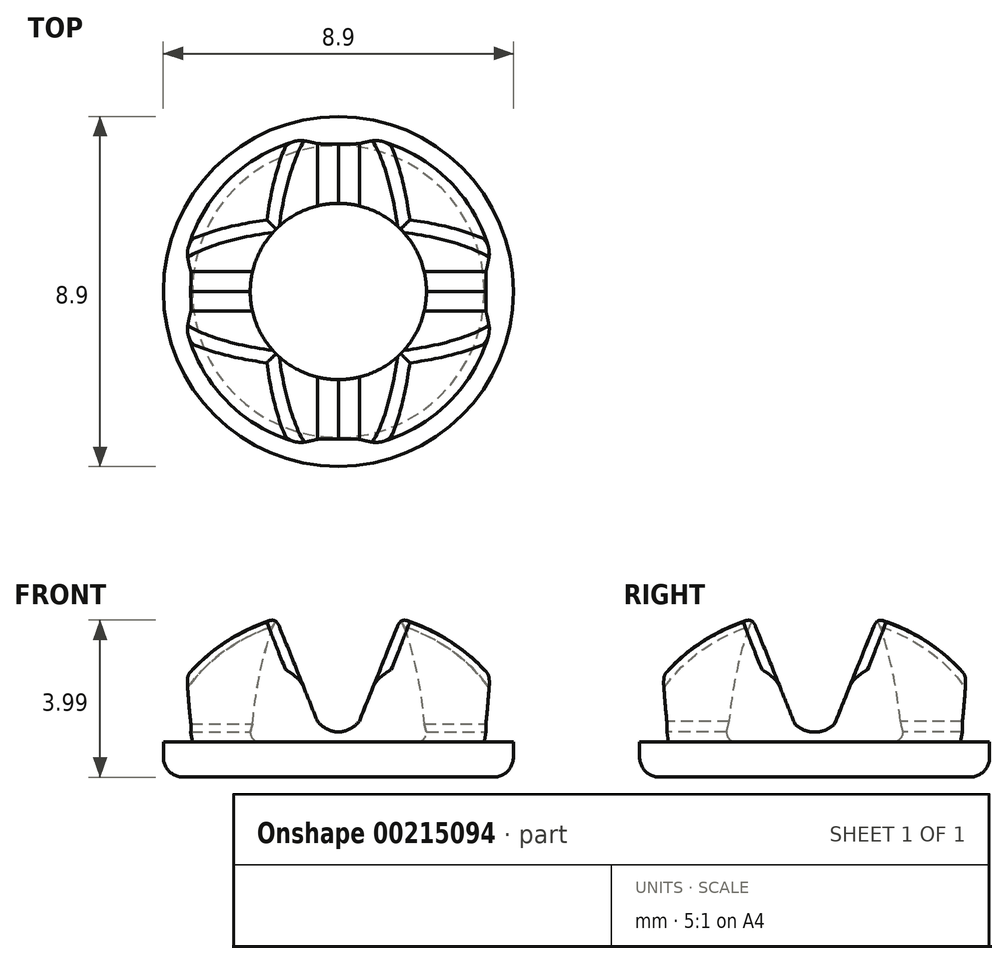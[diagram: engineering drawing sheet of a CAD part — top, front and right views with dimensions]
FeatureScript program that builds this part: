
annotation { "Feature Type Name" : "Feature", "Feature Type Description" : "" }
export const myFeature = defineFeature(function(context is Context, id is Id, definition is map)
    precondition{}
    {
        {
            var Q0;
            Q0=qCreatedBy(makeId("Front.planeOp"),FACE);
            var sketch = newSketch(context, id + "F0", { "sketchPlane" : qUnion([Q0])});
            skLineSegment(sketch, "E0.bottom", {"start": v(0, 0) * mm, "end": v(4.45, 0) * mm});
            skLineSegment(sketch, "E0.top", {"start": v(0, -0.89) * mm, "end": v(4.45, -0.89) * mm});
            skLineSegment(sketch, "E0.left", {"start": v(0, 0) * mm, "end": v(0, -0.89) * mm});
            skLineSegment(sketch, "E0.right", {"start": v(4.45, 0) * mm, "end": v(4.45, -0.89) * mm});
            skLineSegment(sketch, "E1", {"start": v(3.7, 0) * mm, "end": v(3.99, 1.76) * mm});
            skArc(sketch, "E2", {"start": v(3.99, 1.76) * mm, "mid": v(2.24, 3.2) * mm, "end": v(0, 3.56) * mm});
            skLineSegment(sketch, "E3", {"start": v(0, 3.56) * mm, "end": v(0, 0) * mm});
            skSolve(sketch);
        }
        {
            var Q0;
            Q0 = qSketchRegion(id + "F0", true);
            var Q1;
            Q1=sQuery(id+"F0.wireOp",EDGE,"E0.left");
            revolve(context, id + "F1", {"entities" : qUnion([Q0]), "axis" : qUnion([Q1]), "revolveType" : RevolveType.FULL});
        }
        {
            var Q0;
            Q0=qCreatedBy(makeId("Front.planeOp"),FACE);
            var sketch = newSketch(context, id + "F2", { "sketchPlane" : qUnion([Q0])});
            skLineSegment(sketch, "E4", {"start": v(0.46, 0.35) * mm, "end": v(1.77, 3.62) * mm});
            skLineSegment(sketch, "E5", {"start": v(1.77, 3.62) * mm, "end": v(0, 3.62) * mm});
            skLineSegment(sketch, "E6", {"start": v(0, 3.62) * mm, "end": v(0, 0.25) * mm});
            skLineSegment(sketch, "E7.MirrorCS", {"start": v(-1.77, 3.62) * mm, "end": v(0, 3.62) * mm});
            skLineSegment(sketch, "E8.MirrorCS", {"start": v(-0.46, 0.35) * mm, "end": v(-1.77, 3.62) * mm});
            skArc(sketch, "E9", {"start": v(0, 0.25) * mm, "mid": v(0.3, 0.34) * mm, "end": v(0.53, 0.53) * mm});
            skArc(sketch, "E10.MirrorCS", {"start": v(0, 0.25) * mm, "mid": v(-0.3, 0.34) * mm, "end": v(-0.53, 0.53) * mm});
            skSolve(sketch);
        }
        {
            var Q0;
            Q0 = qSketchRegion(id + "F2", true);
            extrude(context, id + "F3", {"entities" : qUnion([Q0]), "operationType" : NewBodyOperationType.REMOVE, "endBound" : BoundingType.THROUGH_ALL, "oppositeDirection" : true, "depth" : 25.4 * mm, "hasSecondDirection" : true, "secondDirectionBound" : SecondDirectionBoundingType.THROUGH_ALL, "secondDirectionOppositeDirection" : false, "secondDirectionDepth" : 25.4 * mm});
        }
        {
            var Q0;
            Q0=qCreatedBy(makeId("Right.planeOp"),FACE);
            var sketch = newSketch(context, id + "F4", { "sketchPlane" : qUnion([Q0])});
            skLineSegment(sketch, "E11", {"start": v(0.46, 0.35) * mm, "end": v(1.78, 3.62) * mm});
            skLineSegment(sketch, "E12", {"start": v(1.78, 3.62) * mm, "end": v(0, 3.62) * mm});
            skLineSegment(sketch, "E13", {"start": v(0, 3.62) * mm, "end": v(0, 0.25) * mm});
            skLineSegment(sketch, "E14.MirrorCS", {"start": v(-1.77, 3.62) * mm, "end": v(0, 3.62) * mm});
            skLineSegment(sketch, "E15.MirrorCS", {"start": v(-0.46, 0.35) * mm, "end": v(-1.77, 3.62) * mm});
            skArc(sketch, "E16", {"start": v(0, 0.25) * mm, "mid": v(0.27, 0.3) * mm, "end": v(0.5, 0.46) * mm});
            skArc(sketch, "E17.MirrorCS", {"start": v(0, 0.25) * mm, "mid": v(-0.27, 0.3) * mm, "end": v(-0.5, 0.46) * mm});
            skSolve(sketch);
        }
        {
            var Q0;
            Q0 = qSketchRegion(id + "F4", true);
            extrude(context, id + "F5", {"entities" : qUnion([Q0]), "operationType" : NewBodyOperationType.REMOVE, "endBound" : BoundingType.THROUGH_ALL, "oppositeDirection" : true, "depth" : 25.4 * mm, "hasSecondDirection" : true, "secondDirectionBound" : SecondDirectionBoundingType.THROUGH_ALL, "secondDirectionOppositeDirection" : false, "secondDirectionDepth" : 25.4 * mm});
        }
        {
            var Q0;
            Q0=qCreatedBy(makeId("Top.planeOp"),FACE);
            cPlane(context, id + "F6", {"entities" : qUnion([Q0]), "cplaneType" : CPlaneType.OFFSET, "offset" : 5.08 * mm, "width" : 152.4 * mm, "height" : 152.4 * mm});
        }
        {
            var Q0;
            Q0=qCreatedBy(id+"F6.planeOp",FACE);
            var sketch = newSketch(context, id + "F7", { "sketchPlane" : qUnion([Q0])});
            skCircle(sketch, "E18", {"center": v(0, 0) * mm, "radius": 2.24 * mm});
            skSolve(sketch);
        }
        {
            var Q0;
            Q0 = qSketchRegion(id + "F7", true);
            extrude(context, id + "F8", {"entities" : qUnion([Q0]), "operationType" : NewBodyOperationType.REMOVE, "oppositeDirection" : true, "depth" : 5.08 * mm});
        }
        {
            var Q0;
            Q0=makeQuery(id+"F8.boolean.opBoolean","COPY",EDGE,{"derivedFrom":makeQuery(id+"F8.opExtrude","CAP_EDGE",EDGE,{"disambiguationData":[OSD([sQuery(id+"F7.wireOp",EDGE,"E18")])],"isStart":false})});
            var Q1;
            {var subQ0=makeQuery(id+"F1.opRevolve","SWEPT_FACE",FACE,{"disambiguationData":[OSD([sQuery(id+"F0.wireOp",EDGE,"E2")])]});var subQ1=makeQuery(id+"F3.opExtrude","SWEPT_FACE",FACE,{"disambiguationData":[OSD([sQuery(id+"F2.wireOp",EDGE,"E8.MirrorCS")])]});Q1=makeQuery(id+"F5.boolean.opBoolean","SPLIT",EDGE,{"disambiguationData":[TD([makeQuery(id+"F5.opExtrude","SWEPT_FACE",FACE,{"disambiguationData":[OSD([sQuery(id+"F4.wireOp",EDGE,"E11")])]})])],"derivedFrom":makeQuery(id+"F3.boolean.opBoolean","INTERSECT",EDGE,{"derivedFrom":[subQ0,subQ1]})});}
            var Q2;
            Q2=makeQuery(id+"F5.boolean.opBoolean","INTERSECT",EDGE,{"derivedFrom":[makeQuery(id+"F3.boolean.opBoolean","SPLIT",FACE,{"disambiguationData":[TD([makeQuery(id+"F3.opExtrude","SWEPT_FACE",FACE,{"disambiguationData":[OSD([sQuery(id+"F2.wireOp",EDGE,"E8.MirrorCS")])]})])],"derivedFrom":makeQuery(id+"F1.opRevolve","SWEPT_FACE",FACE,{"disambiguationData":[OSD([sQuery(id+"F0.wireOp",EDGE,"E2")])]})}),makeQuery(id+"F5.opExtrude","SWEPT_FACE",FACE,{"disambiguationData":[OSD([sQuery(id+"F4.wireOp",EDGE,"E11")])]})]});
            var Q3;
            Q3=makeQuery(id+"F5.boolean.opBoolean","INTERSECT",EDGE,{"derivedFrom":[makeQuery(id+"F3.boolean.opBoolean","SPLIT",FACE,{"disambiguationData":[TD([makeQuery(id+"F3.opExtrude","SWEPT_FACE",FACE,{"disambiguationData":[OSD([sQuery(id+"F2.wireOp",EDGE,"E8.MirrorCS")])]})])],"derivedFrom":makeQuery(id+"F1.opRevolve","SWEPT_FACE",FACE,{"disambiguationData":[OSD([sQuery(id+"F0.wireOp",EDGE,"E2")])]})}),makeQuery(id+"F5.opExtrude","SWEPT_FACE",FACE,{"disambiguationData":[OSD([sQuery(id+"F4.wireOp",EDGE,"E15.MirrorCS")])]})]});
            var Q4;
            Q4=makeQuery(id+"F5.boolean.opBoolean","INTERSECT",EDGE,{"derivedFrom":[makeQuery(id+"F3.boolean.opBoolean","SPLIT",FACE,{"disambiguationData":[TD([makeQuery(id+"F3.opExtrude","SWEPT_FACE",FACE,{"disambiguationData":[OSD([sQuery(id+"F2.wireOp",EDGE,"E4")])]})])],"derivedFrom":makeQuery(id+"F1.opRevolve","SWEPT_FACE",FACE,{"disambiguationData":[OSD([sQuery(id+"F0.wireOp",EDGE,"E2")])]})}),makeQuery(id+"F5.opExtrude","SWEPT_FACE",FACE,{"disambiguationData":[OSD([sQuery(id+"F4.wireOp",EDGE,"E15.MirrorCS")])]})]});
            var Q5;
            {var subQ0=makeQuery(id+"F1.opRevolve","SWEPT_FACE",FACE,{"disambiguationData":[OSD([sQuery(id+"F0.wireOp",EDGE,"E2")])]});var subQ1=makeQuery(id+"F3.opExtrude","SWEPT_FACE",FACE,{"disambiguationData":[OSD([sQuery(id+"F2.wireOp",EDGE,"E4")])]});Q5=makeQuery(id+"F5.boolean.opBoolean","SPLIT",EDGE,{"disambiguationData":[TD([makeQuery(id+"F5.opExtrude","SWEPT_FACE",FACE,{"disambiguationData":[OSD([sQuery(id+"F4.wireOp",EDGE,"E15.MirrorCS")])]})])],"derivedFrom":makeQuery(id+"F3.boolean.opBoolean","INTERSECT",EDGE,{"derivedFrom":[subQ0,subQ1]})});}
            var Q6;
            {var subQ0=makeQuery(id+"F1.opRevolve","SWEPT_FACE",FACE,{"disambiguationData":[OSD([sQuery(id+"F0.wireOp",EDGE,"E2")])]});var subQ1=makeQuery(id+"F3.opExtrude","SWEPT_FACE",FACE,{"disambiguationData":[OSD([sQuery(id+"F2.wireOp",EDGE,"E4")])]});Q6=makeQuery(id+"F5.boolean.opBoolean","SPLIT",EDGE,{"disambiguationData":[TD([makeQuery(id+"F5.opExtrude","SWEPT_FACE",FACE,{"disambiguationData":[OSD([sQuery(id+"F4.wireOp",EDGE,"E11")])]})])],"derivedFrom":makeQuery(id+"F3.boolean.opBoolean","INTERSECT",EDGE,{"derivedFrom":[subQ0,subQ1]})});}
            var Q7;
            Q7=makeQuery(id+"F5.boolean.opBoolean","INTERSECT",EDGE,{"derivedFrom":[makeQuery(id+"F3.boolean.opBoolean","SPLIT",FACE,{"disambiguationData":[TD([makeQuery(id+"F3.opExtrude","SWEPT_FACE",FACE,{"disambiguationData":[OSD([sQuery(id+"F2.wireOp",EDGE,"E4")])]})])],"derivedFrom":makeQuery(id+"F1.opRevolve","SWEPT_FACE",FACE,{"disambiguationData":[OSD([sQuery(id+"F0.wireOp",EDGE,"E2")])]})}),makeQuery(id+"F5.opExtrude","SWEPT_FACE",FACE,{"disambiguationData":[OSD([sQuery(id+"F4.wireOp",EDGE,"E11")])]})]});
            var Q8;
            {var subQ0=makeQuery(id+"F1.opRevolve","SWEPT_FACE",FACE,{"disambiguationData":[OSD([sQuery(id+"F0.wireOp",EDGE,"E2")])]});var subQ1=makeQuery(id+"F3.opExtrude","SWEPT_FACE",FACE,{"disambiguationData":[OSD([sQuery(id+"F2.wireOp",EDGE,"E8.MirrorCS")])]});Q8=makeQuery(id+"F5.boolean.opBoolean","SPLIT",EDGE,{"disambiguationData":[TD([makeQuery(id+"F5.opExtrude","SWEPT_FACE",FACE,{"disambiguationData":[OSD([sQuery(id+"F4.wireOp",EDGE,"E15.MirrorCS")])]})])],"derivedFrom":makeQuery(id+"F3.boolean.opBoolean","INTERSECT",EDGE,{"derivedFrom":[subQ0,subQ1]})});}
            var Q9;
            {var subQ0=sQuery(id+"F0.wireOp",EDGE,"E1");var subQ2=sQuery(id+"F0.wireOp",EDGE,"E2");var subQ4=makeQuery(id+"F3.opExtrude","SWEPT_FACE",FACE,{"disambiguationData":[OSD([sQuery(id+"F2.wireOp",EDGE,"E4")])]});Q9=makeQuery(id+"F5.boolean.opBoolean","SPLIT",EDGE,{"disambiguationData":[TD([makeQuery(id+"F5.opExtrude","SWEPT_FACE",FACE,{"disambiguationData":[OSD([sQuery(id+"F4.wireOp",EDGE,"E15.MirrorCS")])]})])],"derivedFrom":makeQuery(id+"F3.boolean.opBoolean","SPLIT",EDGE,{"disambiguationData":[TD([subQ4])],"derivedFrom":makeQuery(id+"F1.opRevolve","SWEPT_EDGE",EDGE,{"disambiguationData":[OSD([subQ0,subQ2])]})})});}
            var Q10;
            {var subQ0=sQuery(id+"F0.wireOp",EDGE,"E1");var subQ2=sQuery(id+"F0.wireOp",EDGE,"E2");var subQ4=makeQuery(id+"F3.opExtrude","SWEPT_FACE",FACE,{"disambiguationData":[OSD([sQuery(id+"F2.wireOp",EDGE,"E8.MirrorCS")])]});Q10=makeQuery(id+"F5.boolean.opBoolean","SPLIT",EDGE,{"disambiguationData":[TD([makeQuery(id+"F5.opExtrude","SWEPT_FACE",FACE,{"disambiguationData":[OSD([sQuery(id+"F4.wireOp",EDGE,"E15.MirrorCS")])]})])],"derivedFrom":makeQuery(id+"F3.boolean.opBoolean","SPLIT",EDGE,{"disambiguationData":[TD([subQ4])],"derivedFrom":makeQuery(id+"F1.opRevolve","SWEPT_EDGE",EDGE,{"disambiguationData":[OSD([subQ0,subQ2])]})})});}
            var Q11;
            {var subQ0=sQuery(id+"F0.wireOp",EDGE,"E1");var subQ2=sQuery(id+"F0.wireOp",EDGE,"E2");var subQ4=makeQuery(id+"F3.opExtrude","SWEPT_FACE",FACE,{"disambiguationData":[OSD([sQuery(id+"F2.wireOp",EDGE,"E4")])]});Q11=makeQuery(id+"F5.boolean.opBoolean","SPLIT",EDGE,{"disambiguationData":[TD([makeQuery(id+"F5.opExtrude","SWEPT_FACE",FACE,{"disambiguationData":[OSD([sQuery(id+"F4.wireOp",EDGE,"E11")])]})])],"derivedFrom":makeQuery(id+"F3.boolean.opBoolean","SPLIT",EDGE,{"disambiguationData":[TD([subQ4])],"derivedFrom":makeQuery(id+"F1.opRevolve","SWEPT_EDGE",EDGE,{"disambiguationData":[OSD([subQ0,subQ2])]})})});}
            var Q12;
            {var subQ0=sQuery(id+"F0.wireOp",EDGE,"E1");var subQ2=sQuery(id+"F0.wireOp",EDGE,"E2");var subQ4=makeQuery(id+"F3.opExtrude","SWEPT_FACE",FACE,{"disambiguationData":[OSD([sQuery(id+"F2.wireOp",EDGE,"E8.MirrorCS")])]});Q12=makeQuery(id+"F5.boolean.opBoolean","SPLIT",EDGE,{"disambiguationData":[TD([makeQuery(id+"F5.opExtrude","SWEPT_FACE",FACE,{"disambiguationData":[OSD([sQuery(id+"F4.wireOp",EDGE,"E11")])]})])],"derivedFrom":makeQuery(id+"F3.boolean.opBoolean","SPLIT",EDGE,{"disambiguationData":[TD([subQ4])],"derivedFrom":makeQuery(id+"F1.opRevolve","SWEPT_EDGE",EDGE,{"disambiguationData":[OSD([subQ0,subQ2])]})})});}
            fillet(context, id + "F9", {"entities" : qUnion([Q0, Q1, Q2, Q3, Q4, Q5, Q6, Q7, Q8, Q9, Q10, Q11, Q12]), "radius" : 0.25 * mm, "tangentPropagation" : true, "allowEdgeOverflow" : false});
        }
        {
            var Q0;
            Q0=makeQuery(id+"F1.opRevolve","SWEPT_EDGE",EDGE,{"disambiguationData":[OSD([sQuery(id+"F0.wireOp",EDGE,"E0.top"),sQuery(id+"F0.wireOp",EDGE,"E0.right")])]});
            fillet(context, id + "F10", {"entities" : qUnion([Q0]), "radius" : 0.5 * mm, "tangentPropagation" : true, "allowEdgeOverflow" : false});
        }
    });
